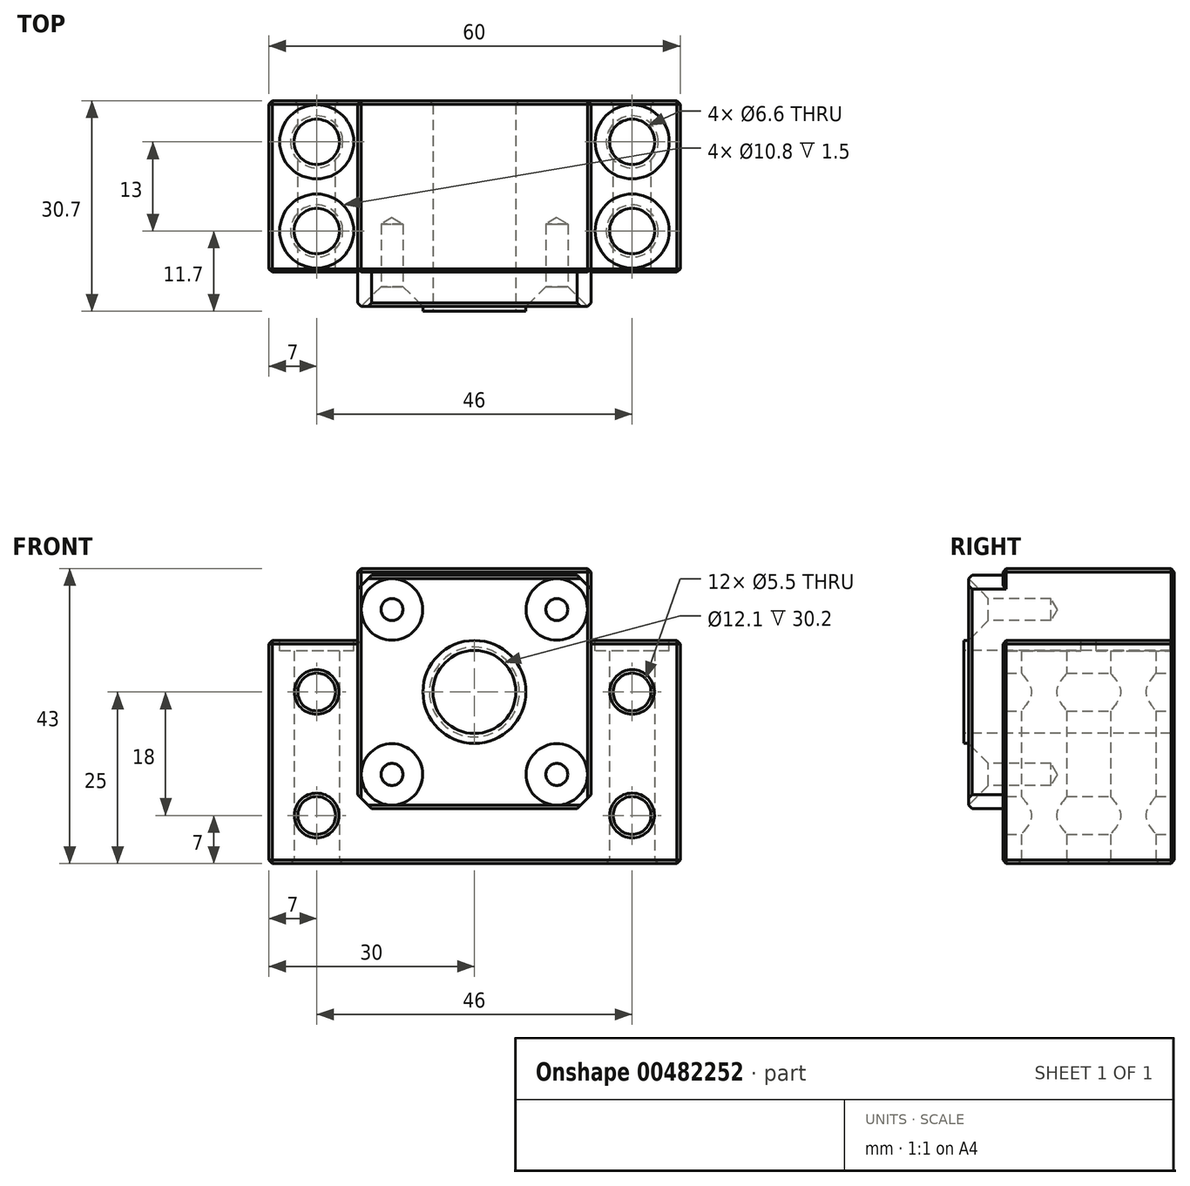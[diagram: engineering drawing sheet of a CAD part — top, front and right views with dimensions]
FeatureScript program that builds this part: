
annotation { "Feature Type Name" : "Feature", "Feature Type Description" : "" }
export const myFeature = defineFeature(function(context is Context, id is Id, definition is map)
    precondition{}
    {
        {
            var Q0;
            Q0=qCreatedBy(makeId("Front.planeOp"),FACE);
            var sketch = newSketch(context, id + "F0", { "sketchPlane" : qUnion([Q0])});
            skCircle(sketch, "E0", {"center": v(0, 0) * mm, "radius": 6.05 * mm});
            skCircle(sketch, "E1", {"center": v(0, 0) * mm, "radius": 7.5 * mm});
            skSolve(sketch);
        }
        {
            var Q0;
            Q0=qCreatedBy(makeId("Front.planeOp"),FACE);
            var sketch = newSketch(context, id + "F1", { "sketchPlane" : qUnion([Q0])});
            skLineSegment(sketch, "E2", {"start": v(-30, 7.5) * mm, "end": v(-30, -25) * mm});
            skLineSegment(sketch, "E3", {"start": v(-30, -25) * mm, "end": v(30, -25) * mm});
            skLineSegment(sketch, "E4", {"start": v(30, -25) * mm, "end": v(30, 7.5) * mm});
            skLineSegment(sketch, "E5", {"start": v(30, 7.5) * mm, "end": v(17, 7.5) * mm});
            skLineSegment(sketch, "E6", {"start": v(17, 7.5) * mm, "end": v(17, 18) * mm});
            skLineSegment(sketch, "E7", {"start": v(17, 18) * mm, "end": v(-17, 18) * mm});
            skLineSegment(sketch, "E8", {"start": v(-17, 18) * mm, "end": v(-17, 7.5) * mm});
            skLineSegment(sketch, "E9", {"start": v(-17, 7.5) * mm, "end": v(-30, 7.5) * mm});
            skLineSegment(sketch, "E10", {"start": v(0, 18) * mm, "end": v(0, -25) * mm, "construction": true});
            skCircle(sketch, "E11", {"center": v(-23, 0) * mm, "radius": 2.75 * mm});
            skCircle(sketch, "E12", {"center": v(-23, -18) * mm, "radius": 2.75 * mm});
            skCircle(sketch, "E13", {"center": v(23, -18) * mm, "radius": 2.75 * mm});
            skCircle(sketch, "E14", {"center": v(23, 0) * mm, "radius": 2.75 * mm});
            skSolve(sketch);
        }
        {
            var Q0;
            Q0=qSketchRegion(id+"F1",true);
            extrude(context, id + "F2", {"entities" : qUnion([Q0]), "depth" : 25 * mm});
        }
        {
            var Q0;
            Q0=makeQuery(id+"F2.opExtrude","CAP_FACE",FACE,{"disambiguationData":[OSD([sQuery(id+"F1.wireOp",EDGE,"E2"),sQuery(id+"F1.wireOp",EDGE,"E3"),sQuery(id+"F1.wireOp",EDGE,"E4"),sQuery(id+"F1.wireOp",EDGE,"E5"),sQuery(id+"F1.wireOp",EDGE,"E6"),sQuery(id+"F1.wireOp",EDGE,"E7"),sQuery(id+"F1.wireOp",EDGE,"E8"),sQuery(id+"F1.wireOp",EDGE,"E9"),sQuery(id+"F1.wireOp",EDGE,"E11"),sQuery(id+"F1.wireOp",EDGE,"E12"),sQuery(id+"F1.wireOp",EDGE,"E13"),sQuery(id+"F1.wireOp",EDGE,"E14")])],"isStart":false});
            var sketch = newSketch(context, id + "F3", { "sketchPlane" : qUnion([Q0])});
            skLineSegment(sketch, "E15.bottom", {"start": v(17, 17) * mm, "end": v(-17, 17) * mm});
            skLineSegment(sketch, "E15.top", {"start": v(17, -17) * mm, "end": v(-17, -17) * mm});
            skLineSegment(sketch, "E15.left", {"start": v(17, 17) * mm, "end": v(17, -17) * mm});
            skLineSegment(sketch, "E15.right", {"start": v(-17, 17) * mm, "end": v(-17, -17) * mm});
            skPoint(sketch, "E15.middle", {"position": v(0, 0) * mm});
            skSolve(sketch);
        }
        {
            var Q0;
            Q0=qSketchRegion(id+"F3",true);
            extrude(context, id + "F4", {"entities" : qUnion([Q0]), "operationType" : NewBodyOperationType.ADD, "depth" : 5 * mm});
        }
        {
            var Q0;
            Q0=makeQuery(id+"F4.opExtrude","CAP_FACE",FACE,{"disambiguationData":[OSD([sQuery(id+"F3.wireOp",EDGE,"E15.bottom"),sQuery(id+"F3.wireOp",EDGE,"E15.top"),sQuery(id+"F3.wireOp",EDGE,"E15.left"),sQuery(id+"F3.wireOp",EDGE,"E15.right")])],"isStart":false});
            var sketch = newSketch(context, id + "F5", { "sketchPlane" : qUnion([Q0])});
            skCircle(sketch, "E16", {"center": v(0, 0) * mm, "radius": 17 * mm, "construction": true});
            skLineSegment(sketch, "E17", {"start": v(-17, 17) * mm, "end": v(17, -17) * mm, "construction": true});
            skLineSegment(sketch, "E18", {"start": v(17, 17) * mm, "end": v(-17, -17) * mm, "construction": true});
            skPoint(sketch, "E19", {"position": v(-12.02, 12.02) * mm});
            skPoint(sketch, "E20", {"position": v(12.02, 12.02) * mm});
            skPoint(sketch, "E21", {"position": v(12.02, -12.02) * mm});
            skPoint(sketch, "E22", {"position": v(-12.02, -12.02) * mm});
            skSolve(sketch);
        }
        {
            var Q0;
            Q0=sQuery(id+"F5.wireOp",VERTEX,"E19");
            var Q1;
            Q1=sQuery(id+"F5.wireOp",VERTEX,"E20");
            var Q2;
            Q2=sQuery(id+"F5.wireOp",VERTEX,"E21");
            var Q3;
            Q3=sQuery(id+"F5.wireOp",VERTEX,"E22");
            var Q4;
            Q4=makeQuery(id+"F2.opExtrude","SWEPT_BODY",BODY,{"disambiguationData":[OSD([sQuery(id+"F1.wireOp",EDGE,"E2"),sQuery(id+"F1.wireOp",EDGE,"E3"),sQuery(id+"F1.wireOp",EDGE,"E4"),sQuery(id+"F1.wireOp",EDGE,"E5"),sQuery(id+"F1.wireOp",EDGE,"E6"),sQuery(id+"F1.wireOp",EDGE,"E7"),sQuery(id+"F1.wireOp",EDGE,"E8"),sQuery(id+"F1.wireOp",EDGE,"E9"),sQuery(id+"F1.wireOp",EDGE,"E11"),sQuery(id+"F1.wireOp",EDGE,"E12"),sQuery(id+"F1.wireOp",EDGE,"E13"),sQuery(id+"F1.wireOp",EDGE,"E14")])]});
            hole(context, id + "F6", {"style" : HoleStyle.C_SINK, "endStyle" : HoleEndStyle.BLIND, "standardTappedOrClearance" : lookupTablePath({ "standard" : "ISO", "engagement" : "75%", "pitch" : "0.75 mm", "size" : "M4", "type" : "Tapped" }), "standardBlindInLast" : lookupTablePath({ "standard" : "ISO", "engagement" : "75%", "pitch" : "0.75 mm", "size" : "M4", "type" : "Tapped" }), "holeDiameter" : 3.2 * mm, "cSinkDiameter" : 8.96 * mm, "cSinkAngle" : 90 * degree, "holeDepth" : 12 * mm, "locations" : qUnion([Q0, Q1, Q2, Q3]), "scope" : qUnion([Q4])});
        }
        {
            var Q0;
            Q0=makeQuery(id+"F4.opExtrude","CAP_FACE",FACE,{"disambiguationData":[OSD([sQuery(id+"F3.wireOp",EDGE,"E15.bottom"),sQuery(id+"F3.wireOp",EDGE,"E15.top"),sQuery(id+"F3.wireOp",EDGE,"E15.left"),sQuery(id+"F3.wireOp",EDGE,"E15.right")])],"isStart":false});
            var sketch = newSketch(context, id + "F7", { "sketchPlane" : qUnion([Q0])});
            skCircle(sketch, "E23", {"center": v(0, 0) * mm, "radius": 6.05 * mm});
            skSolve(sketch);
        }
        {
            var Q0;
            Q0=qSketchRegion(id+"F7",true);
            extrude(context, id + "F8", {"entities" : qUnion([Q0]), "operationType" : NewBodyOperationType.REMOVE, "endBound" : BoundingType.UP_TO_NEXT, "oppositeDirection" : true, "depth" : 25 * mm});
        }
        {
            var Q0;
            Q0=qSketchRegion(id+"F0",true);
            extrude(context, id + "F9", {"entities" : qUnion([Q0]), "operationType" : NewBodyOperationType.ADD, "depth" : 30.7 * mm});
        }
        {
            var Q0;
            Q0=makeQuery(id+"F2.opExtrude","SWEPT_FACE",FACE,{"disambiguationData":[OSD([sQuery(id+"F1.wireOp",EDGE,"E3")])]});
            var sketch = newSketch(context, id + "F10", { "sketchPlane" : qUnion([Q0])});
            skLineSegment(sketch, "E24", {"start": v(0, 25) * mm, "end": v(0, 0) * mm, "construction": true});
            skLineSegment(sketch, "E25", {"start": v(-30, 12.5) * mm, "end": v(30, 12.5) * mm, "construction": true});
            skCircle(sketch, "E26", {"center": v(-23, 19) * mm, "radius": 3.3 * mm});
            skCircle(sketch, "E27", {"center": v(-23, 6) * mm, "radius": 3.3 * mm});
            skCircle(sketch, "E28", {"center": v(23, 6) * mm, "radius": 3.3 * mm});
            skCircle(sketch, "E29", {"center": v(23, 19) * mm, "radius": 3.3 * mm});
            skSolve(sketch);
        }
        {
            var Q0;
            Q0=qSketchRegion(id+"F10",true);
            var Q1;
            Q1=makeQuery(id+"F2.opExtrude","SWEPT_FACE",FACE,{"disambiguationData":[OSD([sQuery(id+"F1.wireOp",EDGE,"E9")])]});
            extrude(context, id + "F11", {"entities" : qUnion([Q0]), "operationType" : NewBodyOperationType.REMOVE, "endBound" : BoundingType.UP_TO_SURFACE, "oppositeDirection" : true, "endBoundEntityFace" : qUnion([Q1]), "depth" : 25 * mm});
        }
        {
            var Q0;
            Q0=makeQuery(id+"F2.opExtrude","CAP_FACE",FACE,{"disambiguationData":[OSD([sQuery(id+"F1.wireOp",EDGE,"E2"),sQuery(id+"F1.wireOp",EDGE,"E3"),sQuery(id+"F1.wireOp",EDGE,"E4"),sQuery(id+"F1.wireOp",EDGE,"E5"),sQuery(id+"F1.wireOp",EDGE,"E6"),sQuery(id+"F1.wireOp",EDGE,"E7"),sQuery(id+"F1.wireOp",EDGE,"E8"),sQuery(id+"F1.wireOp",EDGE,"E9"),sQuery(id+"F1.wireOp",EDGE,"E11"),sQuery(id+"F1.wireOp",EDGE,"E12"),sQuery(id+"F1.wireOp",EDGE,"E13"),sQuery(id+"F1.wireOp",EDGE,"E14")])],"isStart":true});
            var Q1;
            Q1=makeQuery(id+"F2.opExtrude","SWEPT_FACE",FACE,{"disambiguationData":[OSD([sQuery(id+"F1.wireOp",EDGE,"E7")])]});
            var Q2;
            Q2=makeQuery(id+"F2.opExtrude","SWEPT_FACE",FACE,{"disambiguationData":[OSD([sQuery(id+"F1.wireOp",EDGE,"E4")])]});
            var Q3;
            Q3=makeQuery(id+"F2.opExtrude","SWEPT_FACE",FACE,{"disambiguationData":[OSD([sQuery(id+"F1.wireOp",EDGE,"E2")])]});
            var Q4;
            Q4=makeQuery(id+"F2.opExtrude","SWEPT_FACE",FACE,{"disambiguationData":[OSD([sQuery(id+"F1.wireOp",EDGE,"E3")])]});
            var Q5;
            Q5=makeQuery(id+"F2.opExtrude","CAP_EDGE",EDGE,{"disambiguationData":[OSD([sQuery(id+"F1.wireOp",EDGE,"E5")])],"isStart":false});
            var Q6;
            Q6=makeQuery(id+"F2.opExtrude","CAP_EDGE",EDGE,{"disambiguationData":[OSD([sQuery(id+"F1.wireOp",EDGE,"E9")])],"isStart":false});
            var Q7;
            Q7=makeQuery(id+"F2.opExtrude","CAP_EDGE",EDGE,{"disambiguationData":[OSD([sQuery(id+"F1.wireOp",EDGE,"E6")])],"isStart":false});
            var Q8;
            Q8=makeQuery(id+"F2.opExtrude","CAP_EDGE",EDGE,{"disambiguationData":[OSD([sQuery(id+"F1.wireOp",EDGE,"E8")])],"isStart":false});
            var Q9;
            Q9=makeQuery(id+"F2.opExtrude","CAP_EDGE",EDGE,{"disambiguationData":[OSD([sQuery(id+"F1.wireOp",EDGE,"E11")])],"isStart":false});
            var Q10;
            Q10=makeQuery(id+"F2.opExtrude","CAP_EDGE",EDGE,{"disambiguationData":[OSD([sQuery(id+"F1.wireOp",EDGE,"E12")])],"isStart":false});
            var Q11;
            Q11=makeQuery(id+"F2.opExtrude","CAP_EDGE",EDGE,{"disambiguationData":[OSD([sQuery(id+"F1.wireOp",EDGE,"E13")])],"isStart":false});
            var Q12;
            Q12=makeQuery(id+"F2.opExtrude","CAP_EDGE",EDGE,{"disambiguationData":[OSD([sQuery(id+"F1.wireOp",EDGE,"E14")])],"isStart":false});
            var Q13;
            Q13=makeQuery(id+"F4.opExtrude","CAP_EDGE",EDGE,{"disambiguationData":[OSD([sQuery(id+"F3.wireOp",EDGE,"E15.right")])],"isStart":false});
            var Q14;
            Q14=makeQuery(id+"F4.opExtrude","CAP_EDGE",EDGE,{"disambiguationData":[OSD([sQuery(id+"F3.wireOp",EDGE,"E15.left")])],"isStart":false});
            var Q15;
            Q15=makeQuery(id+"F4.opExtrude","CAP_EDGE",EDGE,{"disambiguationData":[OSD([sQuery(id+"F3.wireOp",EDGE,"E15.top")])],"isStart":false});
            var Q16;
            Q16=makeQuery(id+"F4.opExtrude","CAP_EDGE",EDGE,{"disambiguationData":[OSD([sQuery(id+"F3.wireOp",EDGE,"E15.bottom")])],"isStart":false});
            chamfer(context, id + "F12", {"entities" : qUnion([Q0, Q1, Q2, Q3, Q4, Q5, Q6, Q7, Q8, Q9, Q10, Q11, Q12, Q13, Q14, Q15, Q16]), "width" : 0.5 * mm, "tangentPropagation" : true});
        }
        {
            var Q0;
            Q0=makeQuery(id+"F4.opExtrude","SWEPT_EDGE",EDGE,{"disambiguationData":[OSD([sQuery(id+"F3.wireOp",EDGE,"E15.bottom"),sQuery(id+"F3.wireOp",EDGE,"E15.right")])]});
            var Q1;
            Q1=makeQuery(id+"F4.opExtrude","SWEPT_EDGE",EDGE,{"disambiguationData":[OSD([sQuery(id+"F3.wireOp",EDGE,"E15.bottom"),sQuery(id+"F3.wireOp",EDGE,"E15.left")])]});
            var Q2;
            Q2=makeQuery(id+"F4.opExtrude","SWEPT_EDGE",EDGE,{"disambiguationData":[OSD([sQuery(id+"F3.wireOp",EDGE,"E15.top"),sQuery(id+"F3.wireOp",EDGE,"E15.left")])]});
            var Q3;
            Q3=makeQuery(id+"F4.opExtrude","SWEPT_EDGE",EDGE,{"disambiguationData":[OSD([sQuery(id+"F3.wireOp",EDGE,"E15.top"),sQuery(id+"F3.wireOp",EDGE,"E15.right")])]});
            chamfer(context, id + "F13", {"entities" : qUnion([Q0, Q1, Q2, Q3]), "width" : 2 * mm, "tangentPropagation" : true});
        }
        {
            var Q0;
            Q0=makeQuery(id+"F2.opExtrude","SWEPT_FACE",FACE,{"disambiguationData":[OSD([sQuery(id+"F1.wireOp",EDGE,"E9")])]});
            var sketch = newSketch(context, id + "F14", { "sketchPlane" : qUnion([Q0])});
            skCircle(sketch, "E30", {"center": v(-23, -6) * mm, "radius": 5.4 * mm});
            skCircle(sketch, "E31", {"center": v(-23, -19) * mm, "radius": 5.4 * mm});
            skCircle(sketch, "E32", {"center": v(23, -19) * mm, "radius": 5.4 * mm});
            skCircle(sketch, "E33", {"center": v(23, -6) * mm, "radius": 5.4 * mm});
            skSolve(sketch);
        }
        {
            var Q0;
            Q0=qSketchRegion(id+"F14",true);
            extrude(context, id + "F15", {"entities" : qUnion([Q0]), "operationType" : NewBodyOperationType.REMOVE, "oppositeDirection" : true, "depth" : 1.5 * mm});
        }
    });
